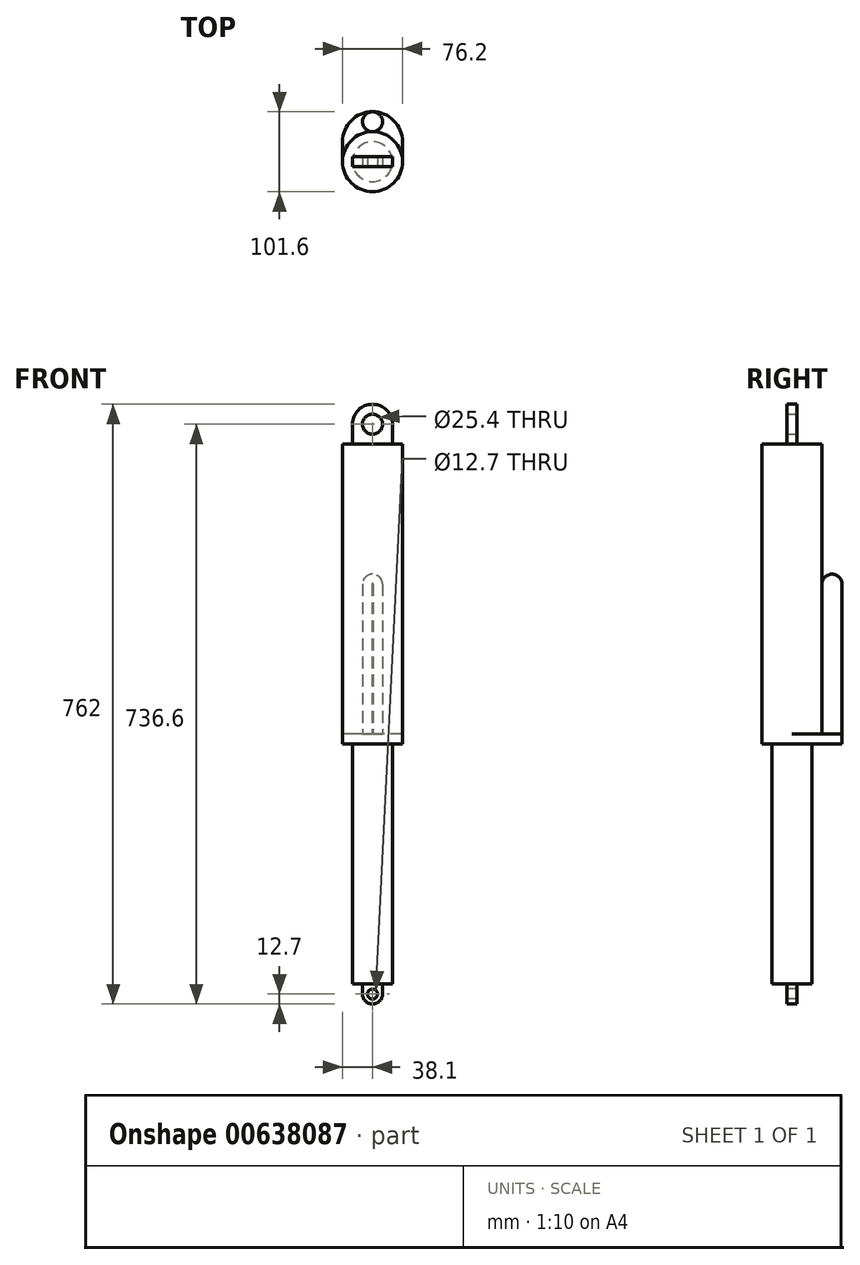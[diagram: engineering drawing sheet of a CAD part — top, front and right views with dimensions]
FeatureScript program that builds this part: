
annotation { "Feature Type Name" : "Feature", "Feature Type Description" : "" }
export const myFeature = defineFeature(function(context is Context, id is Id, definition is map)
    precondition{}
    {
        {
            var Q0;
            Q0=qCreatedBy(makeId("Top.planeOp"),FACE);
            var sketch = newSketch(context, id + "F0", { "sketchPlane" : qUnion([Q0])});
            skCircle(sketch, "E0", {"center": v(0, 0) * mm, "radius": 38.1 * mm});
            skSolve(sketch);
        }
        {
            var Q0;
            Q0=makeQuery(id+"F0.imprint","IMPRINT",FACE,{"disambiguationData":[TD([[makeQuery(id+"F0.imprint","IMPRINT",EDGE,{"derivedFrom":sQuery(id+"F0.wireOp",EDGE,"E0")}),1.0]])]});
            extrude(context, id + "F1", {"entities" : qUnion([Q0]), "depth" : 381 * mm, "offsetDistance" : 25.4 * mm});
        }
        {
            var Q0;
            Q0=qCreatedBy(makeId("Top.planeOp"),FACE);
            var sketch = newSketch(context, id + "F2", { "sketchPlane" : qUnion([Q0])});
            skCircle(sketch, "E1", {"center": v(0, 0) * mm, "radius": 25.4 * mm});
            skSolve(sketch);
        }
        {
            var Q0;
            Q0=makeQuery(id+"F2.imprint","IMPRINT",FACE,{"disambiguationData":[TD([[makeQuery(id+"F2.imprint","IMPRINT",EDGE,{"derivedFrom":sQuery(id+"F2.wireOp",EDGE,"E1")}),1.0]])]});
            extrude(context, id + "F3", {"entities" : qUnion([Q0]), "operationType" : NewBodyOperationType.ADD, "oppositeDirection" : true, "depth" : 304.8 * mm, "offsetDistance" : 25.4 * mm});
        }
        {
            var Q0;
            Q0=qCreatedBy(makeId("Top.planeOp"),FACE);
            var sketch = newSketch(context, id + "F4", { "sketchPlane" : qUnion([Q0])});
            skLineSegment(sketch, "E2.bottom", {"start": v(0, 0) * mm, "end": v(38.1, 0) * mm});
            skLineSegment(sketch, "E2.top", {"start": v(0, 63.5) * mm, "end": v(38.1, 63.5) * mm});
            skLineSegment(sketch, "E2.left", {"start": v(0, 0) * mm, "end": v(0, 63.5) * mm});
            skLineSegment(sketch, "E2.right", {"start": v(38.1, 0) * mm, "end": v(38.1, 63.5) * mm});
            skLineSegment(sketch, "E3.MirrorCS", {"start": v(0, 63.5) * mm, "end": v(-38.1, 63.5) * mm});
            skLineSegment(sketch, "E4.MirrorCS", {"start": v(-38.1, 0) * mm, "end": v(-38.1, 63.5) * mm});
            skLineSegment(sketch, "E5.MirrorCS", {"start": v(0, 0) * mm, "end": v(-38.1, 0) * mm});
            skSolve(sketch);
        }
        {
            var Q0;
            Q0=makeQuery(id+"F4.imprint","IMPRINT",FACE,{"disambiguationData":[TD([[makeQuery(id+"F4.imprint","IMPRINT",EDGE,{"derivedFrom":sQuery(id+"F4.wireOp",EDGE,"E2.bottom")}),1.0]])]});
            var Q1;
            Q1=makeQuery(id+"F4.imprint","IMPRINT",FACE,{"disambiguationData":[TD([[makeQuery(id+"F4.imprint","IMPRINT",EDGE,{"derivedFrom":sQuery(id+"F4.wireOp",EDGE,"E2.left")}),1.0]])]});
            extrude(context, id + "F5", {"entities" : qUnion([Q0, Q1]), "operationType" : NewBodyOperationType.ADD, "depth" : 12.7 * mm, "offsetDistance" : 25.4 * mm});
        }
        {
            var Q0;
            Q0=makeQuery(id+"F5.opExtrude","CAP_FACE",FACE,{"disambiguationData":[OSD([sQuery(id+"F4.wireOp",EDGE,"E2.bottom"),sQuery(id+"F4.wireOp",EDGE,"E2.top"),sQuery(id+"F4.wireOp",EDGE,"E2.right"),sQuery(id+"F4.wireOp",EDGE,"E3.MirrorCS"),sQuery(id+"F4.wireOp",EDGE,"E4.MirrorCS"),sQuery(id+"F4.wireOp",EDGE,"E5.MirrorCS")])],"isStart":false});
            var sketch = newSketch(context, id + "F6", { "sketchPlane" : qUnion([Q0])});
            skCircle(sketch, "E6", {"center": v(0, 50.78) * mm, "radius": 12.7 * mm});
            skSolve(sketch);
        }
        {
            var Q0;
            {var subQ0=sQuery(id+"F6.wireOp",EDGE,"E6");var subQ1=makeQuery(id+"F5.boolean.opBoolean","INTERSECT",EDGE,{"derivedFrom":[makeQuery(id+"F1.opExtrude","SWEPT_FACE",FACE,{"disambiguationData":[OSD([sQuery(id+"F0.wireOp",EDGE,"E0")])]}),makeQuery(id+"F5.opExtrude","CAP_FACE",FACE,{"disambiguationData":[OSD([sQuery(id+"F4.wireOp",EDGE,"E2.bottom"),sQuery(id+"F4.wireOp",EDGE,"E2.top"),sQuery(id+"F4.wireOp",EDGE,"E2.right"),sQuery(id+"F4.wireOp",EDGE,"E3.MirrorCS"),sQuery(id+"F4.wireOp",EDGE,"E4.MirrorCS"),sQuery(id+"F4.wireOp",EDGE,"E5.MirrorCS")])],"isStart":false})]});var subQ2=makeQuery(id+"F6.imprint","INTERSECT",VERTEX,{"disambiguationData":[OD(0.0)],"derivedFrom":[subQ1,subQ0]});Q0=makeQuery(id+"F6.imprint","IMPRINT",FACE,{"disambiguationData":[TD([[makeQuery(id+"F6.imprint","IMPRINT",EDGE,{"disambiguationData":[TD([[subQ2,-1.0]])],"derivedFrom":subQ0}),1.0]])]});}
            extrude(context, id + "F7", {"entities" : qUnion([Q0]), "operationType" : NewBodyOperationType.ADD, "depth" : 203.2 * mm, "offsetDistance" : 25.4 * mm});
        }
        {
            var Q0;
            Q0=makeQuery(id+"F5.opExtrude","SWEPT_EDGE",EDGE,{"disambiguationData":[OSD([sQuery(id+"F4.wireOp",EDGE,"E3.MirrorCS"),sQuery(id+"F4.wireOp",EDGE,"E4.MirrorCS")])]});
            var Q1;
            Q1=makeQuery(id+"F5.opExtrude","SWEPT_EDGE",EDGE,{"disambiguationData":[OSD([sQuery(id+"F4.wireOp",EDGE,"E2.top"),sQuery(id+"F4.wireOp",EDGE,"E2.right")])]});
            fillet(context, id + "F8", {"entities" : qUnion([Q0, Q1]), "radius" : 38.1 * mm, "tangentPropagation" : true, "allowEdgeOverflow" : false});
        }
        {
            var Q0;
            Q0=makeQuery(id+"F7.opExtrude","CAP_EDGE",EDGE,{"disambiguationData":[OSD([sQuery(id+"F6.wireOp",EDGE,"E6")])],"isStart":false});
            fillet(context, id + "F9", {"entities" : qUnion([Q0]), "radius" : 12.7 * mm, "tangentPropagation" : true, "allowEdgeOverflow" : false});
        }
        {
            var Q0;
            Q0=makeQuery(id+"F1.opExtrude","CAP_FACE",FACE,{"disambiguationData":[OSD([sQuery(id+"F0.wireOp",EDGE,"E0")])],"isStart":false});
            var sketch = newSketch(context, id + "F10", { "sketchPlane" : qUnion([Q0])});
            skLineSegment(sketch, "E7.bottom", {"start": v(25.4, -6.35) * mm, "end": v(-25.4, -6.35) * mm});
            skLineSegment(sketch, "E7.top", {"start": v(25.4, 6.35) * mm, "end": v(-25.4, 6.35) * mm});
            skLineSegment(sketch, "E7.left", {"start": v(25.4, -6.35) * mm, "end": v(25.4, 6.35) * mm});
            skLineSegment(sketch, "E7.right", {"start": v(-25.4, -6.35) * mm, "end": v(-25.4, 6.35) * mm});
            skPoint(sketch, "E7.middle", {"position": v(0, 0) * mm});
            skSolve(sketch);
        }
        {
            var Q0;
            Q0=makeQuery(id+"F10.imprint","IMPRINT",FACE,{"disambiguationData":[TD([[makeQuery(id+"F10.imprint","IMPRINT",EDGE,{"derivedFrom":sQuery(id+"F10.wireOp",EDGE,"E7.bottom")}),-1.0]])]});
            extrude(context, id + "F11", {"entities" : qUnion([Q0]), "operationType" : NewBodyOperationType.ADD, "depth" : 25.4 * mm, "offsetDistance" : 25.4 * mm});
        }
        {
            var Q0;
            Q0=makeQuery(id+"F11.opExtrude","SWEPT_FACE",FACE,{"disambiguationData":[OSD([sQuery(id+"F10.wireOp",EDGE,"E7.top")])]});
            var sketch = newSketch(context, id + "F12", { "sketchPlane" : qUnion([Q0])});
            skArc(sketch, "E8", {"start": v(25.4, 406.4) * mm, "mid": v(0, 431.8) * mm, "end": v(-25.4, 406.4) * mm});
            skSolve(sketch);
        }
        {
            var Q0;
            Q0=makeQuery(id+"F12.imprint","IMPRINT",FACE,{"disambiguationData":[TD([[makeQuery(id+"F12.imprint","IMPRINT",EDGE,{"derivedFrom":sQuery(id+"F12.wireOp",EDGE,"E8")}),1.0]])]});
            extrude(context, id + "F13", {"entities" : qUnion([Q0]), "operationType" : NewBodyOperationType.ADD, "oppositeDirection" : true, "depth" : 12.7 * mm, "offsetDistance" : 25.4 * mm});
        }
        {
            var Q0;
            {var subQ0=sQuery(id+"F10.wireOp",EDGE,"E7.top");Q0=makeQuery(id+"F13.boolean.opBoolean","MERGE",FACE,{"derivedFrom":[makeQuery(id+"F11.opExtrude","SWEPT_FACE",FACE,{"disambiguationData":[OSD([subQ0])]}),makeQuery(id+"F13.opExtrude","CAP_FACE",FACE,{"disambiguationData":[OSD([subQ0,sQuery(id+"F12.wireOp",EDGE,"E8")])],"isStart":true})]});}
            var sketch = newSketch(context, id + "F14", { "sketchPlane" : qUnion([Q0])});
            skPoint(sketch, "E9", {"position": v(0, 406.4) * mm});
            skSolve(sketch);
        }
        {
            var Q0;
            Q0=sQuery(id+"F14.wireOp",VERTEX,"E9");
            var Q1;
            Q1=makeQuery(id+"F1.opExtrude","SWEPT_BODY",BODY,{"disambiguationData":[OSD([sQuery(id+"F0.wireOp",EDGE,"E0")])]});
            hole(context, id + "F15", {"style" : HoleStyle.SIMPLE, "endStyle" : HoleEndStyle.THROUGH, "holeDiameter" : 25.4 * mm, "majorDiameter" : 6.35 * mm, "isTappedThrough" : true, "tappedDepth" : 12.7 * mm, "tapClearance" : 3, "locations" : qUnion([Q0]), "scope" : qUnion([Q1])});
        }
        {
            var Q0;
            Q0=makeQuery(id+"F3.opExtrude","CAP_FACE",FACE,{"disambiguationData":[OSD([sQuery(id+"F2.wireOp",EDGE,"E1")])],"isStart":false});
            var sketch = newSketch(context, id + "F16", { "sketchPlane" : qUnion([Q0])});
            skLineSegment(sketch, "E10.bottom", {"start": v(12.7, -6.35) * mm, "end": v(-12.7, -6.35) * mm});
            skLineSegment(sketch, "E10.top", {"start": v(12.7, 6.35) * mm, "end": v(-12.7, 6.35) * mm});
            skLineSegment(sketch, "E10.left", {"start": v(12.7, -6.35) * mm, "end": v(12.7, 6.35) * mm});
            skLineSegment(sketch, "E10.right", {"start": v(-12.7, -6.35) * mm, "end": v(-12.7, 6.35) * mm});
            skPoint(sketch, "E10.middle", {"position": v(0, 0) * mm});
            skSolve(sketch);
        }
        {
            var Q0;
            Q0=makeQuery(id+"F16.imprint","IMPRINT",FACE,{"disambiguationData":[TD([[makeQuery(id+"F16.imprint","IMPRINT",EDGE,{"derivedFrom":sQuery(id+"F16.wireOp",EDGE,"E10.bottom")}),-1.0]])]});
            extrude(context, id + "F17", {"entities" : qUnion([Q0]), "operationType" : NewBodyOperationType.ADD, "depth" : 12.7 * mm, "offsetDistance" : 25.4 * mm});
        }
        {
            var Q0;
            Q0=makeQuery(id+"F17.opExtrude","SWEPT_FACE",FACE,{"disambiguationData":[OSD([sQuery(id+"F16.wireOp",EDGE,"E10.top")])]});
            var sketch = newSketch(context, id + "F18", { "sketchPlane" : qUnion([Q0])});
            skArc(sketch, "E11", {"start": v(-12.7, -317.5) * mm, "mid": v(0, -330.2) * mm, "end": v(12.7, -317.5) * mm});
            skSolve(sketch);
        }
        {
            var Q0;
            Q0=makeQuery(id+"F18.imprint","IMPRINT",FACE,{"disambiguationData":[TD([[makeQuery(id+"F18.imprint","IMPRINT",EDGE,{"derivedFrom":sQuery(id+"F18.wireOp",EDGE,"E11")}),1.0]])]});
            extrude(context, id + "F19", {"entities" : qUnion([Q0]), "operationType" : NewBodyOperationType.ADD, "oppositeDirection" : true, "depth" : 12.7 * mm, "offsetDistance" : 25.4 * mm});
        }
        {
            var Q0;
            {var subQ0=sQuery(id+"F16.wireOp",EDGE,"E10.top");Q0=makeQuery(id+"F19.boolean.opBoolean","MERGE",FACE,{"derivedFrom":[makeQuery(id+"F17.opExtrude","SWEPT_FACE",FACE,{"disambiguationData":[OSD([subQ0])]}),makeQuery(id+"F19.opExtrude","CAP_FACE",FACE,{"disambiguationData":[OSD([subQ0,sQuery(id+"F18.wireOp",EDGE,"E11")])],"isStart":true})]});}
            var sketch = newSketch(context, id + "F20", { "sketchPlane" : qUnion([Q0])});
            skPoint(sketch, "E12", {"position": v(0, -317.5) * mm});
            skSolve(sketch);
        }
        {
            var Q0;
            Q0=sQuery(id+"F20.wireOp",VERTEX,"E12");
            var Q1;
            Q1=makeQuery(id+"F1.opExtrude","SWEPT_BODY",BODY,{"disambiguationData":[OSD([sQuery(id+"F0.wireOp",EDGE,"E0")])]});
            hole(context, id + "F21", {"style" : HoleStyle.SIMPLE, "endStyle" : HoleEndStyle.THROUGH, "holeDiameter" : 12.7 * mm, "majorDiameter" : 6.35 * mm, "isTappedThrough" : true, "tappedDepth" : 12.7 * mm, "tapClearance" : 3, "locations" : qUnion([Q0]), "scope" : qUnion([Q1])});
        }
    });
